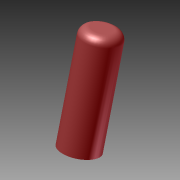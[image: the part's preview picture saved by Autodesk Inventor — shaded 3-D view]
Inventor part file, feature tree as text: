
AUTODESK INVENTOR PART (.ipt)
format: ipt  version: 2011 SP1 (Build 150282100, 282)  size: 85,504 bytes
history: native  units: in
note: dims shown in document units (in); Inventor stores cm internally (conversion verified against a paired STEP export)
features: other x7, revolve x1, sketch x1
ambient origin geometry x8: Origin, YZ Plane, XZ Plane, XY Plane, X Axis, Y Axis, Z Axis, Center Point
bodies: Solid1 (feature_tree)
feature tree (9):
  revolve  "Revolution1"  [1 undecoded]
  other  "to_body_XY"
  other  "to_body_YZ"
  other  "to_body_ZX"
  other  "to_body_X"
  other  "to_body_Y"
  other  "to_body_Z"
  other  "to_body_Center"
  sketch  "Sketch_1"  dims[d0=360.0deg]
note: 1 required parameter value undecoded (feature->parameter linkage not recoverable at this tier; creation-order binding heuristic only, values carry confidence <= 0.55)
